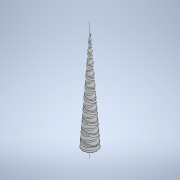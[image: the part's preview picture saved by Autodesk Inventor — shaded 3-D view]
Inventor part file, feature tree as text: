
AUTODESK INVENTOR PART (.ipt)
format: ipt  version: 2022 (Build 260153000, 153)  size: 1,136,128 bytes
history: native  units: in
note: dims shown in document units (in); Inventor stores cm internally (conversion verified against a paired STEP export)
features: sketch x5, other x2, revolve x2, helix x2, fillet x2, extrude x1
ambient origin geometry x8: Origin, YZ Plane, XZ Plane, XY Plane, X Axis, Y Axis, Z Axis, Center Point
bodies: Solid1 (feature_tree)
feature tree (14):
  other  "CrossSection1"
  extrude  "Extrusion1"  Depth=0.1969in
  revolve  "Revolution1"  [1 undecoded]
  sketch  "Sketch3"  dims[d6=0.0787in d7=90.0deg d8=0.4331in d9=0.2362in d10=0.7677in]
  other  "Work Axis2"
  helix  "Coil1"  [1 undecoded]
  revolve  "Revolution2"  Angle=90.0deg
  fillet  "Fillet1"  Radius=0.4331in
  fillet  "Fillet2"  Radius=0.2362in
  helix  "Coil2"  [1 undecoded]
  sketch  "Sketch1"  dims[d0=1.1811in d1=0.1969in]
  sketch  "Sketch2"  dims[d2=0.1181in d3=0.0in d4=7.874in d5=0.0394in]
  sketch  "Sketch4"  dims[d11=0.7618in d12=0.3937in d13=3.937in d14=-0.0275in d15=90.0deg d16=90.0deg d17=0.0in d18=0.0in]
  sketch  "Sketch5"  dims[d19=0.4724in d20=0.2362in d21=0.7677in d22=90.0deg d23=0.0394in d24=0.1969in d26=0.1969in d27=0.1378in d28=0.0591in d29=0.3937in d30=0.3937in d31=7.5984in d32=0.0268in d33=90.0deg d34=90.0deg d35=0.0in d36=0.0in d37=0.0197in d38=0.0787in d39=0.0in d40=0.7874in]
note: 3 required parameter values undecoded (feature->parameter linkage not recoverable at this tier; creation-order binding heuristic only, values carry confidence <= 0.55)